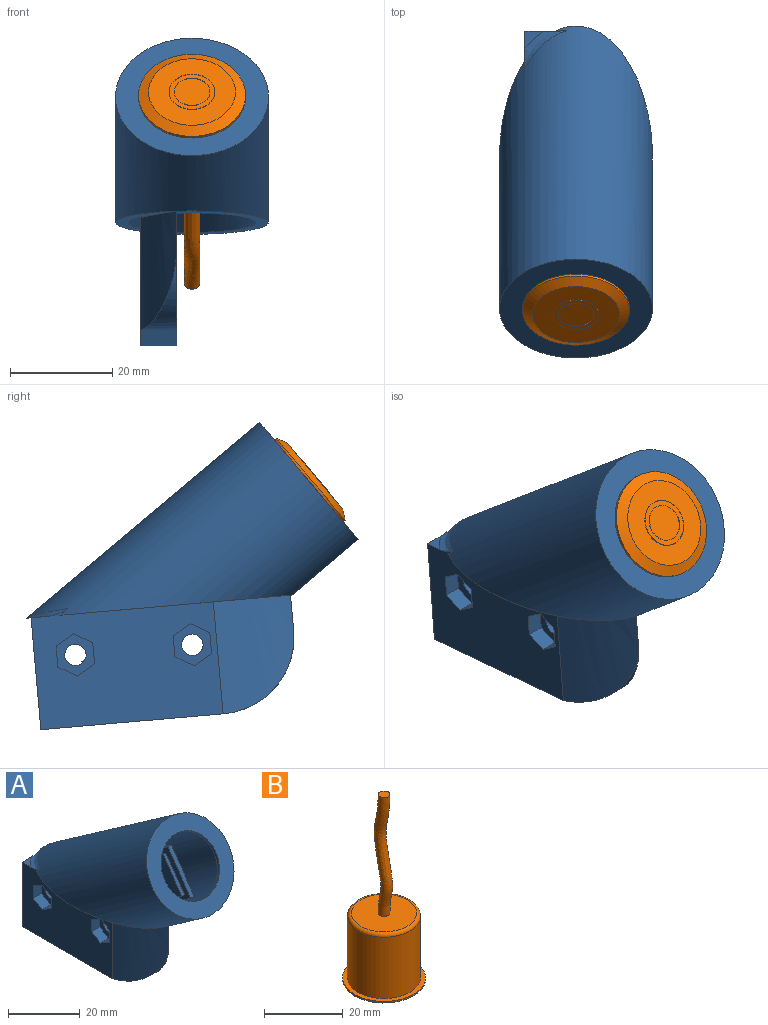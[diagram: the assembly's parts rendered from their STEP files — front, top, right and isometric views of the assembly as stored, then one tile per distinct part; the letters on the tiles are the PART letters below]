
ASSEMBLY  parts=2 mates=1
PART A: 64 faces, bbox 30.5x67.3x59.3 mm
  f0: cylinder r=78.21mm len=22.59mm, axis (0,0,1), area 314.4mm2, adj f1,f8,f11,f12,f13,f16,f32,f62
  f1: plane 36x7mm, normal (0,0,-1), area 252mm2, adj f0,f8,f10,f11,f62
  f2: plane 2.42x1.33mm, normal (0,0,1), area 0.8mm2, adj f26,f33,f53
  f3: plane 0.89x0.54mm, normal (0,0,1), area 0.3mm2, adj f8,f33,f59
  f4: cylinder r=2.1mm len=4.2mm, axis (1,0,0), area 48.8mm2, adj f8,f41
  f5: cylinder r=2.1mm len=4.2mm, axis (1,0,0), area 48.8mm2, adj f8,f34
  f6: plane 3.73x2.11mm, normal (0,0,1), area 4.7mm2, adj f24,f26,f33,f50,f54,f58
  f7: plane 27.07x7mm, normal (0,0,1), area 88.6mm2, adj f8,f11,f26,f28,f30,f31,f32,f33
  f8: plane 61.16x50.54mm, normal (1,0,0), area 1572mm2, adj f0,f1,f3,f4,f5,f7,f10,f12
  f9: plane 3.77x3.35mm, normal (0,0,1), area 5.7mm2, adj f10,f11,f63
  f10: plane 23.03x8.64mm, normal (0,1,0), area 154.3mm2, adj f1,f8,f9,f11,f14,f15,f63
  f11: plane 35.92x25.09mm, normal (-1,0,0), area 705.8mm2, adj f0,f1,f7,f9,f10,f13,f15,f16
  f12: plane 0.28x0.17mm, normal (0,0,1), area 0mm2, adj f0,f8,f15
  f13: plane 45.05x11.83mm, normal (0,0,-1), area 116.8mm2, adj f0,f11,f15,f16
  f14: plane 52.3x19.1mm, normal (0,0,-1), area 214.9mm2, adj f8,f10,f15,f16
  f15: cylinder r=15mm len=66.17mm, axis (0,-0.82,0.57), area 3596.4mm2, adj f10,f11,f12,f13,f14,f19,f63
  f16: cylinder r=12.5mm len=59.52mm, axis (0,-0.82,0.57), area 2874.9mm2, adj f0,f8,f11,f13,f14,f17,f32,f33
  f17: plane 25x20.48mm, normal (0,0.82,-0.57), area 176.7mm2, adj f16,f18
  f18: cylinder r=10mm len=20mm, axis (0,0.82,-0.57), area 62.8mm2, adj f17,f19
  f19: plane 30x24.57mm, normal (0,-0.82,0.57), area 392.7mm2, adj f15,f18
  f20: plane 13x2mm, normal (0,1,0), area 26mm2, adj f8,f21,f29,f31
  f21: plane 6x2mm, normal (0,0,1), area 12mm2, adj f8,f20,f22,f27
  f22: plane 13x2mm, normal (0,-1,0), area 26mm2, adj f8,f21,f24,f25
  f23: plane 11x2mm, normal (1,0,0), area 22mm2, adj f25,f27,f28,f29
  f24: cylinder r=2mm len=2mm, axis (1,0,0), area 6.3mm2, adj f6,f8,f22,f26,f48
  f25: cylinder r=2mm len=13mm, axis (0,0,1), area 37.7mm2, adj f22,f23,f26,f27
  f26: torus R=4mm, axis (0,0,1), area 13.5mm2, adj f2,f6,f7,f24,f25,f28,f33,f55
  f27: cylinder r=2mm len=6mm, axis (0,1,0), area 12.6mm2, adj f21,f23,f25,f29
  f28: cylinder r=2mm len=2mm, axis (0,-1,0), area 6.3mm2, adj f7,f23,f26,f30
  f29: cylinder r=2mm len=13mm, axis (0,0,-1), area 37.7mm2, adj f20,f23,f27,f30
  f30: torus R=4mm, axis (0,0,1), area 13.5mm2, adj f7,f28,f29,f31,f55
  f31: cylinder r=2mm len=2mm, axis (-1,0,0), area 6.3mm2, adj f7,f8,f20,f30,f48
  f32: bspline ~13.3x9.38mm, area 11.7mm2, adj f0,f7,f8,f11,f16
  f33: bspline ~20.47x11.74mm, area 51.4mm2, adj f2,f3,f6,f7,f8,f11,f16,f26
  f34: plane 8.31x7.2mm, normal (-1,0,0), area 31mm2, adj f5,f35,f36,f37,f38,f39,f40
  f35: plane 3.6x3.3mm, normal (0,-0.5,0.87), area 13.7mm2, adj f11,f34,f36,f40
  f36: plane 3.6x3.3mm, normal (0,0.5,0.87), area 13.7mm2, adj f11,f34,f35,f37
  f37: plane 4.16x3.3mm, normal (0,1,0), area 13.7mm2, adj f11,f34,f36,f38
  f38: plane 3.6x3.3mm, normal (0,0.5,-0.87), area 13.7mm2, adj f11,f34,f37,f39
  f39: plane 3.6x3.3mm, normal (0,-0.5,-0.87), area 13.7mm2, adj f11,f34,f38,f40
  f40: plane 4.16x3.3mm, normal (0,-1,0), area 13.7mm2, adj f11,f34,f35,f39
  f41: plane 8.31x7.2mm, normal (-1,0,0), area 31mm2, adj f4,f42,f43,f44,f45,f46,f47
  f42: plane 3.6x3.3mm, normal (0,-0.5,0.87), area 13.7mm2, adj f11,f41,f43,f47
  f43: plane 3.6x3.3mm, normal (0,0.5,0.87), area 13.7mm2, adj f11,f41,f42,f44
  f44: plane 4.16x3.3mm, normal (0,1,0), area 13.7mm2, adj f11,f41,f43,f45
  f45: plane 3.6x3.3mm, normal (0,0.5,-0.87), area 13.7mm2, adj f11,f41,f44,f46
  f46: plane 3.6x3.3mm, normal (0,-0.5,-0.87), area 13.7mm2, adj f11,f41,f45,f47
  f47: plane 4.16x3.3mm, normal (0,-1,0), area 13.7mm2, adj f11,f41,f42,f46
  f48: plane 10x1.36mm, normal (0,0,-1), area 13.6mm2, adj f8,f24,f31,f50
  f49: plane 40.38x28.28mm, normal (0,0.57,0.82), area 66.9mm2, adj f8,f50,f51,f59,f60
  f50: plane 50.24x28.49mm, normal (-1,0,0), area 610.2mm2, adj f6,f7,f33,f48,f49,f51,f52,f60
  f51: plane 13.02x9.12mm, normal (0,-0.82,0.57), area 21.6mm2, adj f8,f49,f50,f52
  f52: plane 19.44x13.61mm, normal (0,-0.57,-0.82), area 32.2mm2, adj f8,f50,f51,f61
  f53: plane 46.46x27.39mm, normal (-1,0,0), area 495.8mm2, adj f2,f7,f33,f54,f55,f56,f57
  f54: plane 39.13x27.41mm, normal (0,0.57,0.82), area 51.5mm2, adj f6,f33,f53,f56,f58
  f55: plane 9.83x1.08mm, normal (0,0,-1), area 10.2mm2, adj f26,f30,f53,f58
  f56: plane 10.53x7.37mm, normal (0,-0.82,0.57), area 13.9mm2, adj f53,f54,f57,f58
  f57: plane 24.08x16.86mm, normal (0,-0.57,-0.82), area 31.7mm2, adj f7,f53,f56,f58
  f58: plane 46.49x27.39mm, normal (1,0,0), area 495.8mm2, adj f6,f7,f54,f55,f56,f57
  f59: cylinder r=1mm len=0.89mm, axis (-1,0,0), area 0.5mm2, adj f3,f8,f49,f60
  f60: bspline ~0.95x0.83mm, area 0.3mm2, adj f33,f49,f50,f59
  f61: cylinder r=1mm len=1.82mm, axis (1,0,0), area 3.4mm2, adj f7,f8,f50,f52
  f62: cylinder r=15mm len=15mm, axis (1,0,0), area 81.7mm2, adj f0,f1,f8
  f63: bspline ~10.17x9.04mm, area 18.7mm2, adj f9,f10,f11,f15
PART B: 13 faces, bbox 21x21x58.4 mm
  f0: cylinder r=9.25mm len=19mm, axis (0,0,-1), area 1104.3mm2, adj f4,f12
  f1: plane 16.5x16.5mm, normal (0,0,1), area 206.8mm2, adj f11,f12
  f2: cylinder r=10.5mm len=21mm, axis (0,0,1), area 33mm2, adj f4,f5
  f3: plane 17x17mm, normal (0,0,-1), area 163.4mm2, adj f5,f7
  f4: plane 21x21mm, normal (0,0,1), area 77.6mm2, adj f0,f2
  f5: cone r=8.5mm half-angle=63.4deg, axis (0,0,1), area 133.5mm2, adj f2,f3
  f6: cylinder r=3.5mm len=7mm, axis (0,0,1), area 2.2mm2, adj f8,f9
  f7: cylinder r=4.5mm len=9mm, axis (0,0,1), area 2.8mm2, adj f3,f8
  f8: plane 9x9mm, normal (0,0,-1), area 25.1mm2, adj f6,f7
  f9: plane 7x7mm, normal (0,0,-1), area 38.5mm2, adj f6
  f10: plane 3x3mm, normal (0,0,1), area 7.1mm2, adj f11
  f11: bspline ~36.78x8.41mm, area 350.1mm2, adj f1,f10
  f12: torus R=8.25mm, axis (0,0,1), area 87.7mm2, adj f0,f1
PLACE A rot(axis=(-1,0,0),5deg) t=(-33.55,15.13,-2.22)mm
PLACE B rot(axis=(-1,0,0),130deg) t=(-30.55,-39.25,24.58)mm
MATE slider B.f0 <-> A.f15  axis (0,-0.77,0.64) through (-30.55,-24.7,12.37)mm
